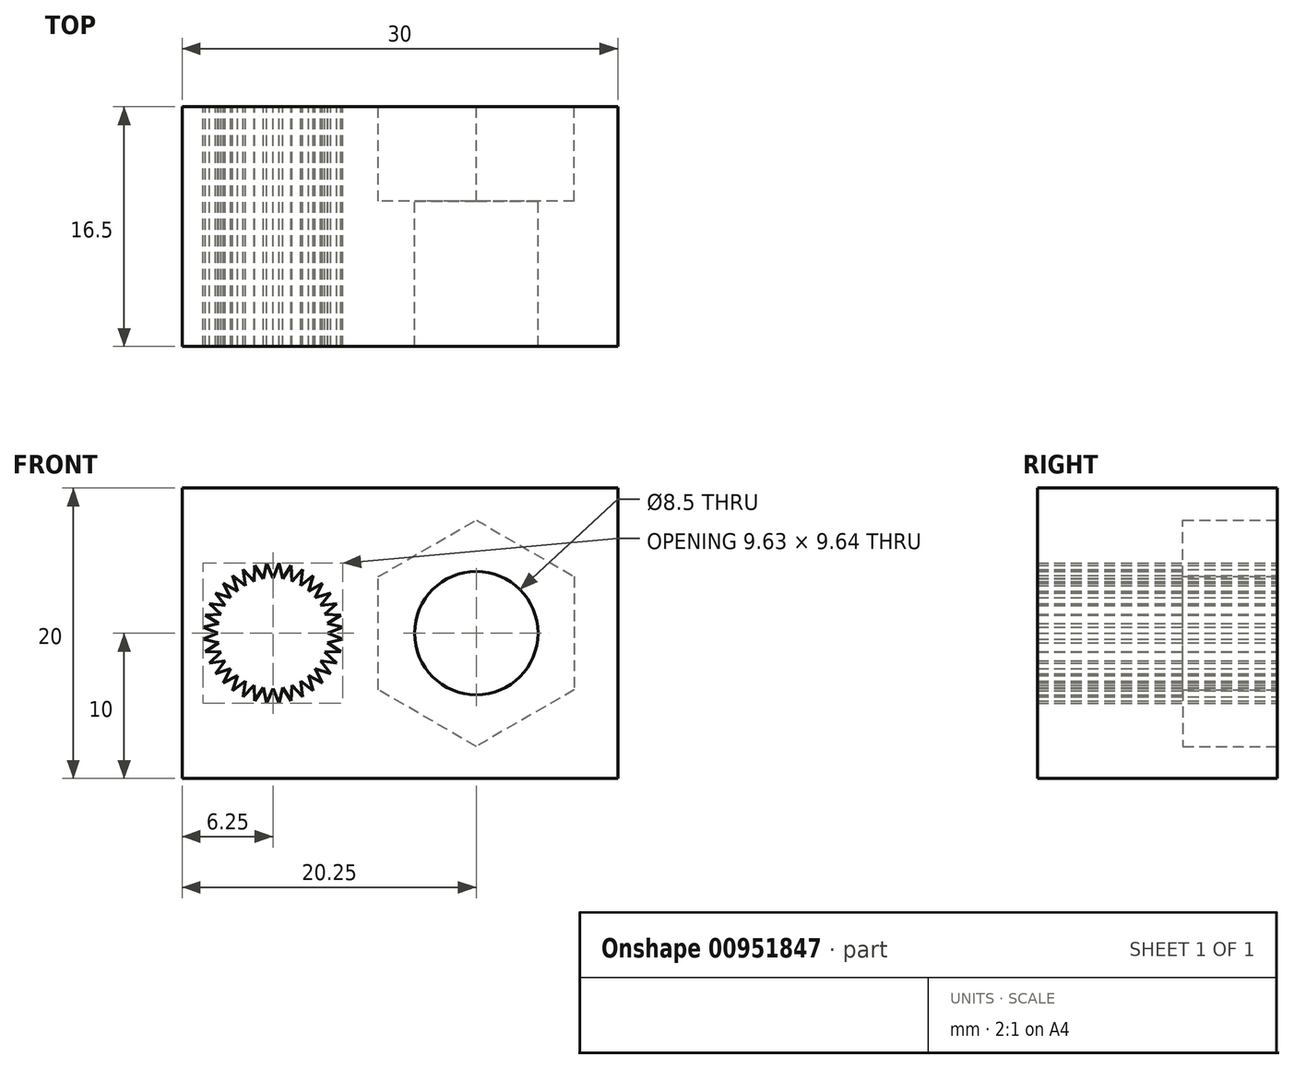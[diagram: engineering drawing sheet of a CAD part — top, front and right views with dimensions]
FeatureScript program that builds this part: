
annotation { "Feature Type Name" : "Feature", "Feature Type Description" : "" }
export const myFeature = defineFeature(function(context is Context, id is Id, definition is map)
    precondition{}
    {
        {
            var Q0;
            Q0=qCreatedBy(makeId("Front.planeOp"),FACE);
            var sketch = newSketch(context, id + "F0", { "sketchPlane" : qUnion([Q0])});
            skLineSegment(sketch, "E0.bottom", {"start": v(0, 0) * mm, "end": v(-30, 0) * mm});
            skLineSegment(sketch, "E0.top", {"start": v(0, 20) * mm, "end": v(-30, 20) * mm});
            skLineSegment(sketch, "E0.left", {"start": v(0, 0) * mm, "end": v(0, 20) * mm});
            skLineSegment(sketch, "E0.right", {"start": v(-30, 0) * mm, "end": v(-30, 20) * mm});
            skCircle(sketch, "E1", {"center": v(-23.75, 10) * mm, "radius": 3.8 * mm});
            skCircle(sketch, "E2.cCircle", {"center": v(-9.75, 10) * mm, "radius": 6.75 * mm, "construction": true});
            skLineSegment(sketch, "E2.0", {"start": v(-9.75, 2.2) * mm, "end": v(-16.5, 6.1) * mm});
            skLineSegment(sketch, "E2.1", {"start": v(-16.5, 6.1) * mm, "end": v(-16.5, 13.9) * mm});
            skLineSegment(sketch, "E2.2", {"start": v(-16.5, 13.9) * mm, "end": v(-9.75, 17.8) * mm});
            skLineSegment(sketch, "E2.3", {"start": v(-9.75, 17.8) * mm, "end": v(-3, 13.9) * mm});
            skLineSegment(sketch, "E2.4", {"start": v(-3, 13.9) * mm, "end": v(-3, 6.1) * mm});
            skLineSegment(sketch, "E2.5", {"start": v(-3, 6.1) * mm, "end": v(-9.75, 2.2) * mm});
            skPoint(sketch, "E2.0.midPoint", {"position": v(-13.12, 4.15) * mm});
            skSolve(sketch);
        }
        {
            var Q0;
            Q0 = qSketchRegion(id + "F0", true);
            extrude(context, id + "F1", {"entities" : qUnion([Q0]), "depth" : 6.5 * mm, "offsetDistance" : 25 * mm});
        }
        {
            var Q0;
            Q0=makeQuery(id+"F1.opExtrude","CAP_FACE",FACE,{"disambiguationData":[OSD([sQuery(id+"F0.wireOp",EDGE,"E0.bottom"),sQuery(id+"F0.wireOp",EDGE,"E0.top"),sQuery(id+"F0.wireOp",EDGE,"E0.left"),sQuery(id+"F0.wireOp",EDGE,"E0.right"),sQuery(id+"F0.wireOp",EDGE,"E1"),sQuery(id+"F0.wireOp",EDGE,"E2.0"),sQuery(id+"F0.wireOp",EDGE,"E2.1"),sQuery(id+"F0.wireOp",EDGE,"E2.2"),sQuery(id+"F0.wireOp",EDGE,"E2.3"),sQuery(id+"F0.wireOp",EDGE,"E2.4"),sQuery(id+"F0.wireOp",EDGE,"E2.5")])],"isStart":false});
            var sketch = newSketch(context, id + "F2", { "sketchPlane" : qUnion([Q0])});
            skLineSegment(sketch, "E3.bottom", {"start": v(-30, 20) * mm, "end": v(0, 20) * mm});
            skLineSegment(sketch, "E3.top", {"start": v(-30, 0) * mm, "end": v(0, 0) * mm});
            skLineSegment(sketch, "E3.left", {"start": v(-30, 20) * mm, "end": v(-30, 0) * mm});
            skLineSegment(sketch, "E3.right", {"start": v(0, 20) * mm, "end": v(0, 0) * mm});
            skCircle(sketch, "E4", {"center": v(-23.75, 10) * mm, "radius": 3.8 * mm});
            skCircle(sketch, "E5", {"center": v(-9.75, 10) * mm, "radius": 4.25 * mm});
            skLineSegment(sketch, "E6", {"start": v(-16.5, 13.9) * mm, "end": v(-3, 6.1) * mm, "construction": true});
            skLineSegment(sketch, "E7", {"start": v(-16.5, 6.1) * mm, "end": v(-3, 13.9) * mm, "construction": true});
            skSolve(sketch);
        }
        {
            var Q0;
            Q0 = qSketchRegion(id + "F2", true);
            extrude(context, id + "F3", {"entities" : qUnion([Q0]), "operationType" : NewBodyOperationType.ADD, "depth" : 10 * mm, "offsetDistance" : 25 * mm});
        }
        {
            var Q0;
            Q0=makeQuery(id+"F1.opExtrude","CAP_FACE",FACE,{"disambiguationData":[OSD([sQuery(id+"F0.wireOp",EDGE,"E0.bottom"),sQuery(id+"F0.wireOp",EDGE,"E0.top"),sQuery(id+"F0.wireOp",EDGE,"E0.left"),sQuery(id+"F0.wireOp",EDGE,"E0.right"),sQuery(id+"F0.wireOp",EDGE,"E1"),sQuery(id+"F0.wireOp",EDGE,"E2.0"),sQuery(id+"F0.wireOp",EDGE,"E2.1"),sQuery(id+"F0.wireOp",EDGE,"E2.2"),sQuery(id+"F0.wireOp",EDGE,"E2.3"),sQuery(id+"F0.wireOp",EDGE,"E2.4"),sQuery(id+"F0.wireOp",EDGE,"E2.5")])],"isStart":true});
            var sketch = newSketch(context, id + "F4", { "sketchPlane" : qUnion([Q0])});
            skCircle(sketch, "E8", {"center": v(23.75, 10) * mm, "radius": 4.84 * mm, "construction": true});
            skLineSegment(sketch, "E9", {"start": v(23.75, 13.8) * mm, "end": v(23.33, 14.82) * mm});
            skLineSegment(sketch, "E10", {"start": v(23.75, 13.8) * mm, "end": v(24.17, 14.82) * mm});
            skLineSegment(sketch, "E11", {"start": v(23.33, 14.82) * mm, "end": v(23.75, 10) * mm, "construction": true});
            skLineSegment(sketch, "E12", {"start": v(24.17, 14.82) * mm, "end": v(23.75, 10) * mm, "construction": true});
            skLineSegment(sketch, "E13", {"start": v(23.75, 10) * mm, "end": v(23.75, 14.84) * mm, "construction": true});
            skLineSegment(sketch, "E14.1.0", {"start": v(23.1, 13.74) * mm, "end": v(22.5, 14.67) * mm});
            skLineSegment(sketch, "E14.1.1", {"start": v(23.1, 13.74) * mm, "end": v(23.33, 14.82) * mm});
            skLineSegment(sketch, "E14.2.0", {"start": v(22.45, 13.57) * mm, "end": v(21.7, 14.38) * mm});
            skLineSegment(sketch, "E14.2.1", {"start": v(22.45, 13.57) * mm, "end": v(22.5, 14.67) * mm});
            skLineSegment(sketch, "E14.3.0", {"start": v(21.85, 13.3) * mm, "end": v(20.98, 13.96) * mm});
            skLineSegment(sketch, "E14.3.1", {"start": v(21.85, 13.3) * mm, "end": v(21.7, 14.38) * mm});
            skLineSegment(sketch, "E14.4.0", {"start": v(21.3, 12.91) * mm, "end": v(20.33, 13.42) * mm});
            skLineSegment(sketch, "E14.4.1", {"start": v(21.3, 12.91) * mm, "end": v(20.98, 13.96) * mm});
            skLineSegment(sketch, "E14.5.0", {"start": v(20.84, 12.44) * mm, "end": v(19.79, 12.77) * mm});
            skLineSegment(sketch, "E14.5.1", {"start": v(20.84, 12.44) * mm, "end": v(20.33, 13.42) * mm});
            skLineSegment(sketch, "E14.6.0", {"start": v(20.46, 11.9) * mm, "end": v(19.37, 12.04) * mm});
            skLineSegment(sketch, "E14.6.1", {"start": v(20.46, 11.9) * mm, "end": v(19.79, 12.77) * mm});
            skLineSegment(sketch, "E14.7.0", {"start": v(20.18, 11.3) * mm, "end": v(19.08, 11.25) * mm});
            skLineSegment(sketch, "E14.7.1", {"start": v(20.18, 11.3) * mm, "end": v(19.37, 12.04) * mm});
            skLineSegment(sketch, "E14.8.0", {"start": v(20, 10.66) * mm, "end": v(18.93, 10.42) * mm});
            skLineSegment(sketch, "E14.8.1", {"start": v(20, 10.66) * mm, "end": v(19.08, 11.25) * mm});
            skLineSegment(sketch, "E14.9.0", {"start": v(19.95, 10) * mm, "end": v(18.93, 9.58) * mm});
            skLineSegment(sketch, "E14.9.1", {"start": v(19.95, 10) * mm, "end": v(18.93, 10.42) * mm});
            skLineSegment(sketch, "E14.10.0", {"start": v(20, 9.34) * mm, "end": v(19.08, 8.75) * mm});
            skLineSegment(sketch, "E14.10.1", {"start": v(20, 9.34) * mm, "end": v(18.93, 9.58) * mm});
            skLineSegment(sketch, "E14.11.0", {"start": v(20.18, 8.7) * mm, "end": v(19.37, 7.96) * mm});
            skLineSegment(sketch, "E14.11.1", {"start": v(20.18, 8.7) * mm, "end": v(19.08, 8.75) * mm});
            skLineSegment(sketch, "E14.12.0", {"start": v(20.46, 8.1) * mm, "end": v(19.79, 7.23) * mm});
            skLineSegment(sketch, "E14.12.1", {"start": v(20.46, 8.1) * mm, "end": v(19.37, 7.96) * mm});
            skLineSegment(sketch, "E14.13.0", {"start": v(20.84, 7.56) * mm, "end": v(20.33, 6.58) * mm});
            skLineSegment(sketch, "E14.13.1", {"start": v(20.84, 7.56) * mm, "end": v(19.79, 7.23) * mm});
            skLineSegment(sketch, "E14.14.0", {"start": v(21.3, 7.09) * mm, "end": v(20.98, 6.04) * mm});
            skLineSegment(sketch, "E14.14.1", {"start": v(21.3, 7.09) * mm, "end": v(20.33, 6.58) * mm});
            skLineSegment(sketch, "E14.15.0", {"start": v(21.85, 6.7) * mm, "end": v(21.7, 5.62) * mm});
            skLineSegment(sketch, "E14.15.1", {"start": v(21.85, 6.7) * mm, "end": v(20.98, 6.04) * mm});
            skLineSegment(sketch, "E14.16.0", {"start": v(22.45, 6.43) * mm, "end": v(22.5, 5.33) * mm});
            skLineSegment(sketch, "E14.16.1", {"start": v(22.45, 6.43) * mm, "end": v(21.7, 5.62) * mm});
            skLineSegment(sketch, "E14.17.0", {"start": v(23.1, 6.26) * mm, "end": v(23.33, 5.18) * mm});
            skLineSegment(sketch, "E14.17.1", {"start": v(23.1, 6.26) * mm, "end": v(22.5, 5.33) * mm});
            skLineSegment(sketch, "E14.18.0", {"start": v(23.75, 6.2) * mm, "end": v(24.17, 5.18) * mm});
            skLineSegment(sketch, "E14.18.1", {"start": v(23.75, 6.2) * mm, "end": v(23.33, 5.18) * mm});
            skLineSegment(sketch, "E14.19.0", {"start": v(24.4, 6.26) * mm, "end": v(25, 5.33) * mm});
            skLineSegment(sketch, "E14.19.1", {"start": v(24.4, 6.26) * mm, "end": v(24.17, 5.18) * mm});
            skLineSegment(sketch, "E14.20.0", {"start": v(25.05, 6.43) * mm, "end": v(25.8, 5.62) * mm});
            skLineSegment(sketch, "E14.20.1", {"start": v(25.05, 6.43) * mm, "end": v(25, 5.33) * mm});
            skLineSegment(sketch, "E14.21.0", {"start": v(25.65, 6.7) * mm, "end": v(26.52, 6.04) * mm});
            skLineSegment(sketch, "E14.21.1", {"start": v(25.65, 6.7) * mm, "end": v(25.8, 5.62) * mm});
            skLineSegment(sketch, "E14.22.0", {"start": v(26.2, 7.09) * mm, "end": v(27.17, 6.58) * mm});
            skLineSegment(sketch, "E14.22.1", {"start": v(26.2, 7.09) * mm, "end": v(26.52, 6.04) * mm});
            skLineSegment(sketch, "E14.23.0", {"start": v(26.66, 7.56) * mm, "end": v(27.71, 7.23) * mm});
            skLineSegment(sketch, "E14.23.1", {"start": v(26.66, 7.56) * mm, "end": v(27.17, 6.58) * mm});
            skLineSegment(sketch, "E14.24.0", {"start": v(27.04, 8.1) * mm, "end": v(28.13, 7.96) * mm});
            skLineSegment(sketch, "E14.24.1", {"start": v(27.04, 8.1) * mm, "end": v(27.71, 7.23) * mm});
            skLineSegment(sketch, "E14.25.0", {"start": v(27.32, 8.7) * mm, "end": v(28.42, 8.75) * mm});
            skLineSegment(sketch, "E14.25.1", {"start": v(27.32, 8.7) * mm, "end": v(28.13, 7.96) * mm});
            skLineSegment(sketch, "E14.26.0", {"start": v(27.5, 9.34) * mm, "end": v(28.57, 9.58) * mm});
            skLineSegment(sketch, "E14.26.1", {"start": v(27.5, 9.34) * mm, "end": v(28.42, 8.75) * mm});
            skLineSegment(sketch, "E14.27.0", {"start": v(27.55, 10) * mm, "end": v(28.57, 10.42) * mm});
            skLineSegment(sketch, "E14.27.1", {"start": v(27.55, 10) * mm, "end": v(28.57, 9.58) * mm});
            skLineSegment(sketch, "E14.28.0", {"start": v(27.5, 10.66) * mm, "end": v(28.42, 11.25) * mm});
            skLineSegment(sketch, "E14.28.1", {"start": v(27.5, 10.66) * mm, "end": v(28.57, 10.42) * mm});
            skLineSegment(sketch, "E14.29.0", {"start": v(27.32, 11.3) * mm, "end": v(28.13, 12.04) * mm});
            skLineSegment(sketch, "E14.29.1", {"start": v(27.32, 11.3) * mm, "end": v(28.42, 11.25) * mm});
            skLineSegment(sketch, "E14.30.0", {"start": v(27.04, 11.9) * mm, "end": v(27.71, 12.77) * mm});
            skLineSegment(sketch, "E14.30.1", {"start": v(27.04, 11.9) * mm, "end": v(28.13, 12.04) * mm});
            skLineSegment(sketch, "E14.31.0", {"start": v(26.66, 12.44) * mm, "end": v(27.17, 13.42) * mm});
            skLineSegment(sketch, "E14.31.1", {"start": v(26.66, 12.44) * mm, "end": v(27.71, 12.77) * mm});
            skLineSegment(sketch, "E14.32.0", {"start": v(26.2, 12.91) * mm, "end": v(26.52, 13.96) * mm});
            skLineSegment(sketch, "E14.32.1", {"start": v(26.2, 12.91) * mm, "end": v(27.17, 13.42) * mm});
            skLineSegment(sketch, "E14.33.0", {"start": v(25.65, 13.3) * mm, "end": v(25.8, 14.38) * mm});
            skLineSegment(sketch, "E14.33.1", {"start": v(25.65, 13.3) * mm, "end": v(26.52, 13.96) * mm});
            skLineSegment(sketch, "E14.34.0", {"start": v(25.05, 13.57) * mm, "end": v(25, 14.67) * mm});
            skLineSegment(sketch, "E14.34.1", {"start": v(25.05, 13.57) * mm, "end": v(25.8, 14.38) * mm});
            skLineSegment(sketch, "E14.35.0", {"start": v(24.4, 13.74) * mm, "end": v(24.17, 14.82) * mm});
            skLineSegment(sketch, "E14.35.1", {"start": v(24.4, 13.74) * mm, "end": v(25, 14.67) * mm});
            skCircle(sketch, "E15", {"center": v(23.75, 10) * mm, "radius": 3.8 * mm});
            skSolve(sketch);
        }
        {
            var Q0;
            Q0 = qSketchRegion(id + "F4", true);
            extrude(context, id + "F5", {"entities" : qUnion([Q0]), "operationType" : NewBodyOperationType.REMOVE, "oppositeDirection" : true, "depth" : 25 * mm, "offsetDistance" : 25 * mm});
        }
    });
